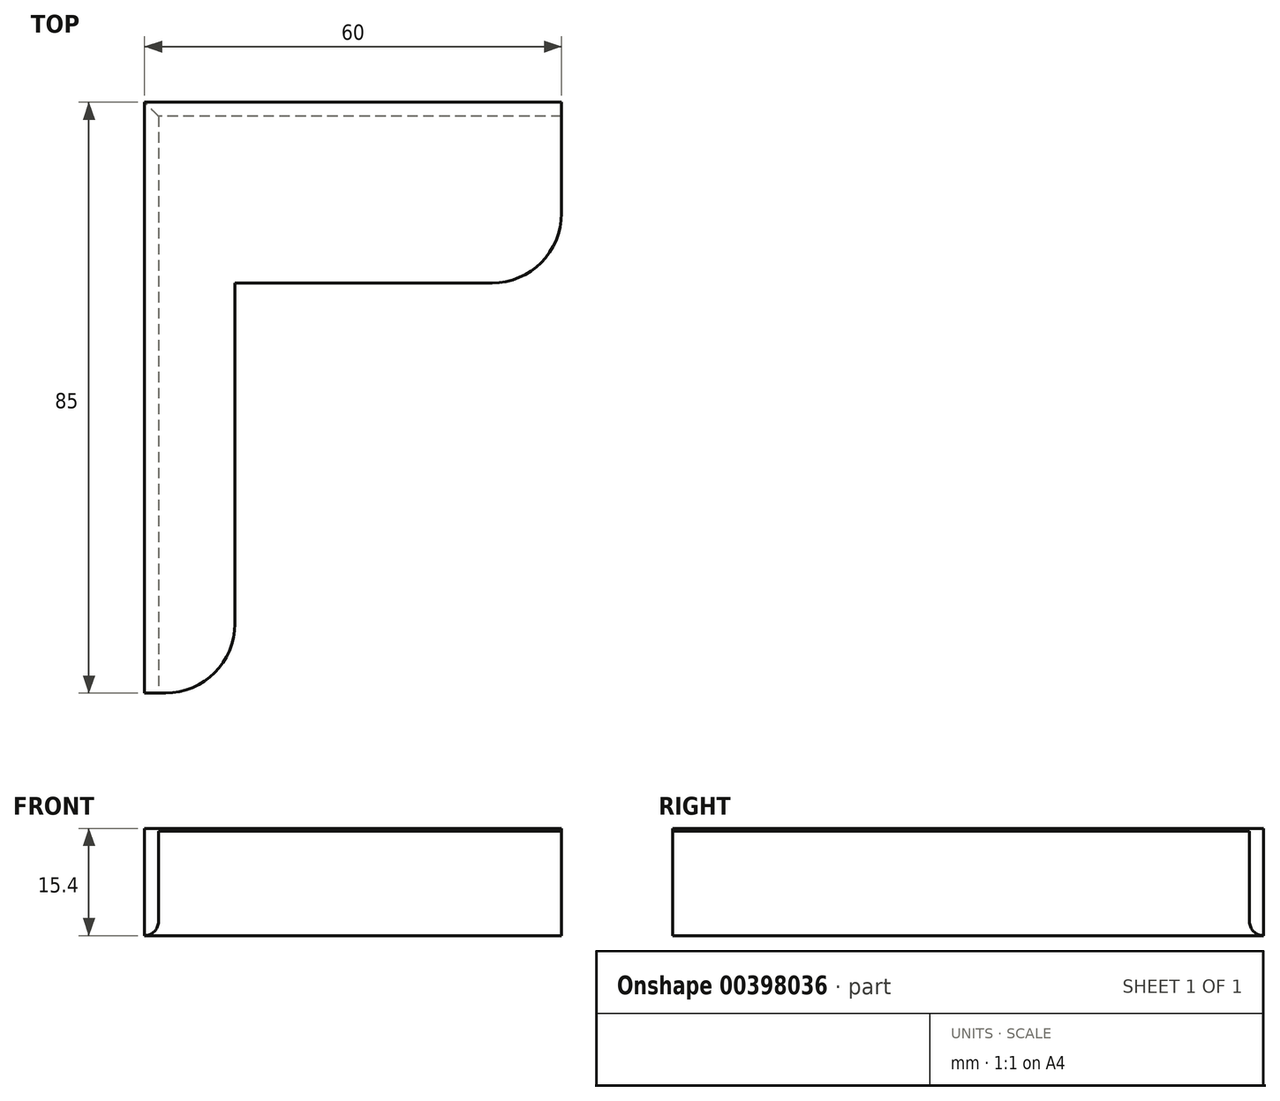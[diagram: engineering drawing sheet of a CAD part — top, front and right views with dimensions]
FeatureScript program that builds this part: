
annotation { "Feature Type Name" : "Feature", "Feature Type Description" : "" }
export const myFeature = defineFeature(function(context is Context, id is Id, definition is map)
    precondition{}
    {
        {
            var Q0;
            Q0=qCreatedBy(makeId("Top.planeOp"),FACE);
            var sketch = newSketch(context, id + "F0", { "sketchPlane" : qUnion([Q0])});
            skLineSegment(sketch, "E0.top", {"start": v(0, -59) * mm, "end": v(-13, -59) * mm});
            skLineSegment(sketch, "E0.left", {"start": v(0, 0) * mm, "end": v(0, -59) * mm});
            skLineSegment(sketch, "E0.right", {"start": v(-13, 0) * mm, "end": v(-13, -59) * mm});
            skLineSegment(sketch, "E1.bottom", {"start": v(0, 0) * mm, "end": v(47, 0) * mm});
            skLineSegment(sketch, "E1.top", {"start": v(-13, 26) * mm, "end": v(47, 26) * mm});
            skLineSegment(sketch, "E1.left", {"start": v(-13, 0) * mm, "end": v(-13, 26) * mm});
            skLineSegment(sketch, "E1.right", {"start": v(47, 0) * mm, "end": v(47, 26) * mm});
            skSolve(sketch);
        }
        {
            var Q0;
            Q0=makeQuery(id+"F0.imprint","IMPRINT",FACE,{"disambiguationData":[TD([[makeQuery(id+"F0.imprint","IMPRINT",EDGE,{"derivedFrom":sQuery(id+"F0.wireOp",EDGE,"E0.top")}),-1.0]])]});
            extrude(context, id + "F1", {"entities" : qUnion([Q0]), "depth" : 0.4 * mm});
        }
        {
            var Q0;
            Q0=makeQuery(id+"F1.opExtrude","CAP_FACE",FACE,{"disambiguationData":[OSD([sQuery(id+"F0.wireOp",EDGE,"E0.top"),sQuery(id+"F0.wireOp",EDGE,"E0.left"),sQuery(id+"F0.wireOp",EDGE,"E0.right"),sQuery(id+"F0.wireOp",EDGE,"E1.bottom"),sQuery(id+"F0.wireOp",EDGE,"E1.top"),sQuery(id+"F0.wireOp",EDGE,"E1.left"),sQuery(id+"F0.wireOp",EDGE,"E1.right")])],"isStart":true});
            var sketch = newSketch(context, id + "F2", { "sketchPlane" : qUnion([Q0])});
            skLineSegment(sketch, "E2.bottom", {"start": v(-13, -26) * mm, "end": v(-11, -26) * mm});
            skLineSegment(sketch, "E2.top", {"start": v(-13, 59) * mm, "end": v(-11, 59) * mm});
            skLineSegment(sketch, "E2.left", {"start": v(-13, -26) * mm, "end": v(-13, 59) * mm});
            skLineSegment(sketch, "E2.right", {"start": v(-11, -24) * mm, "end": v(-11, 59) * mm});
            skLineSegment(sketch, "E3.bottom", {"start": v(47, -26) * mm, "end": v(-11, -26) * mm});
            skLineSegment(sketch, "E3.top", {"start": v(47, -24) * mm, "end": v(-11, -24) * mm});
            skLineSegment(sketch, "E3.left", {"start": v(47, -26) * mm, "end": v(47, -24) * mm});
            skSolve(sketch);
        }
        {
            var Q0;
            Q0=makeQuery(id+"F2.imprint","IMPRINT",FACE,{"disambiguationData":[TD([[makeQuery(id+"F2.imprint","IMPRINT",EDGE,{"derivedFrom":sQuery(id+"F2.wireOp",EDGE,"E2.bottom")}),1.0]])]});
            extrude(context, id + "F3", {"entities" : qUnion([Q0]), "operationType" : NewBodyOperationType.ADD, "depth" : 15 * mm});
        }
        {
            var Q0;
            Q0=makeQuery(id+"F3.opExtrude","CAP_EDGE",EDGE,{"disambiguationData":[OSD([sQuery(id+"F2.wireOp",EDGE,"E2.right")])],"isStart":false});
            var Q1;
            Q1=makeQuery(id+"F3.opExtrude","CAP_EDGE",EDGE,{"disambiguationData":[OSD([sQuery(id+"F2.wireOp",EDGE,"E3.top")])],"isStart":false});
            fillet(context, id + "F4", {"entities" : qUnion([Q0, Q1]), "radius" : 2 * mm, "tangentPropagation" : true, "allowEdgeOverflow" : false});
        }
        {
            var Q0;
            Q0=makeQuery(id+"F1.opExtrude","SWEPT_EDGE",EDGE,{"disambiguationData":[OSD([sQuery(id+"F0.wireOp",EDGE,"E0.top"),sQuery(id+"F0.wireOp",EDGE,"E0.left")])]});
            var Q1;
            Q1=makeQuery(id+"F1.opExtrude","SWEPT_EDGE",EDGE,{"disambiguationData":[OSD([sQuery(id+"F0.wireOp",EDGE,"E1.bottom"),sQuery(id+"F0.wireOp",EDGE,"E1.right")])]});
            fillet(context, id + "F5", {"entities" : qUnion([Q0, Q1]), "radius" : 10 * mm, "tangentPropagation" : true, "allowEdgeOverflow" : false});
        }
    });
